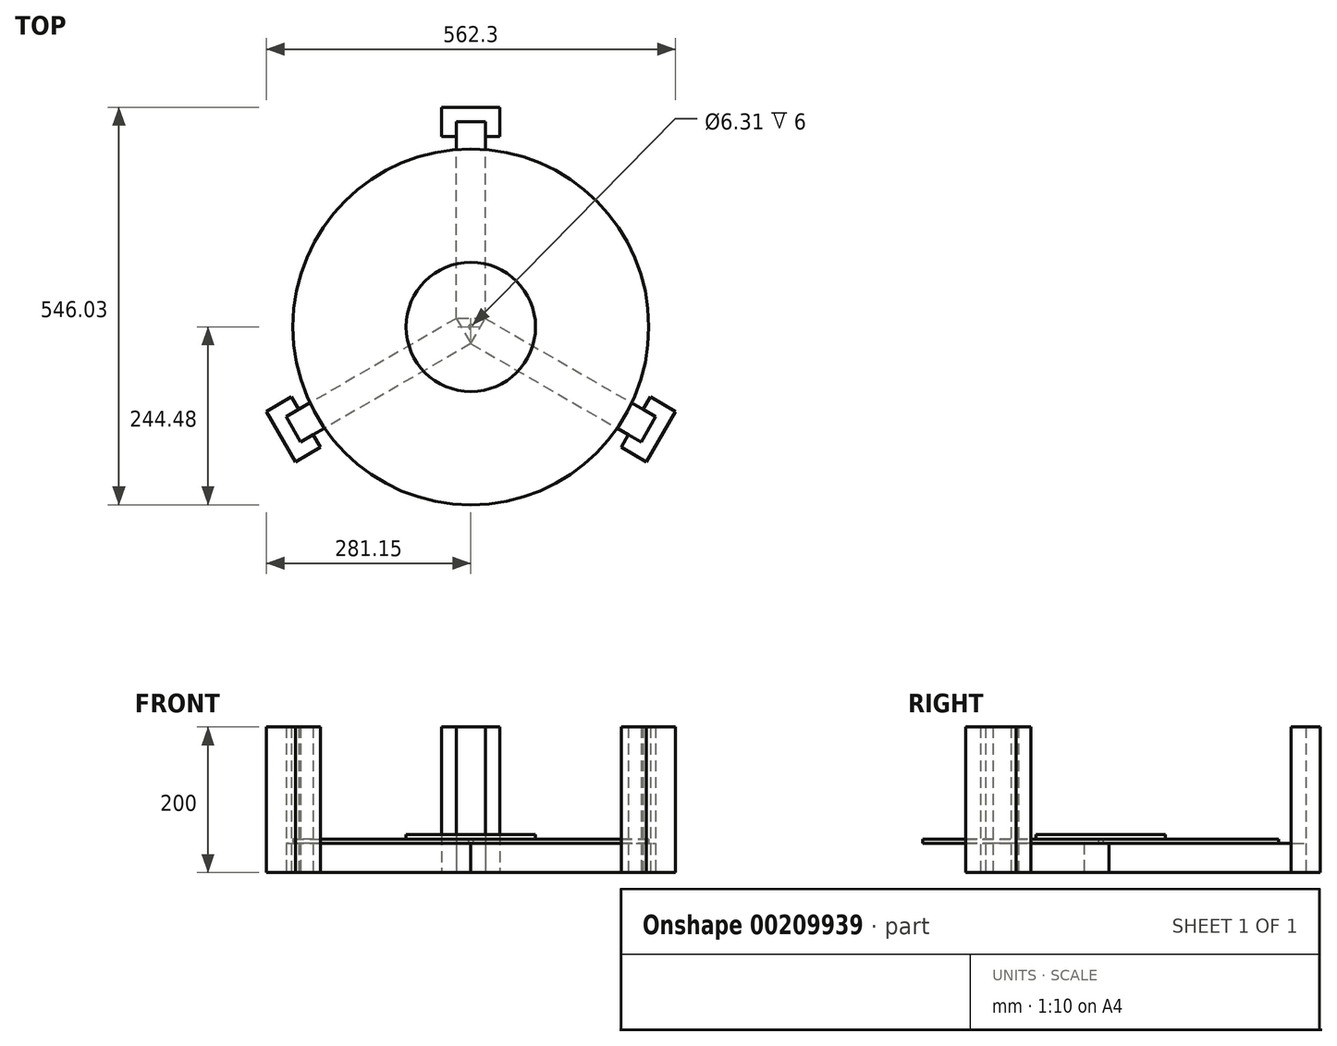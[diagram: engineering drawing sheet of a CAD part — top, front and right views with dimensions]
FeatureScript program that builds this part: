
annotation { "Feature Type Name" : "Feature", "Feature Type Description" : "" }
export const myFeature = defineFeature(function(context is Context, id is Id, definition is map)
    precondition{}
    {
        {
            var Q0;
            Q0=qCreatedBy(makeId("Top.planeOp"),FACE);
            var sketch = newSketch(context, id + "F0", { "sketchPlane" : qUnion([Q0])});
            skLineSegment(sketch, "E0.bottom", {"start": v(0, 0) * mm, "end": v(-20, 0) * mm});
            skLineSegment(sketch, "E0.top", {"start": v(0, 270) * mm, "end": v(-20, 270) * mm});
            skLineSegment(sketch, "E0.left", {"start": v(0, 0) * mm, "end": v(0, 270) * mm});
            skLineSegment(sketch, "E0.right", {"start": v(-20, 0) * mm, "end": v(-20, 270) * mm});
            skLineSegment(sketch, "E1.bottom", {"start": v(0, 0) * mm, "end": v(20, 0) * mm});
            skLineSegment(sketch, "E1.top", {"start": v(0, 270) * mm, "end": v(20, 270) * mm});
            skLineSegment(sketch, "E1.right", {"start": v(20, 0) * mm, "end": v(20, 270) * mm});
            skSolve(sketch);
        }
        {
            var Q0;
            Q0=makeQuery(id+"F0.imprint","IMPRINT",FACE,{"disambiguationData":[TD([[makeQuery(id+"F0.imprint","IMPRINT",EDGE,{"derivedFrom":sQuery(id+"F0.wireOp",EDGE,"E0.bottom")}),-1.0]])]});
            var Q1;
            Q1=makeQuery(id+"F0.imprint","IMPRINT",FACE,{"disambiguationData":[TD([[makeQuery(id+"F0.imprint","IMPRINT",EDGE,{"derivedFrom":sQuery(id+"F0.wireOp",EDGE,"E1.bottom")}),1.0]])]});
            extrude(context, id + "F1", {"entities" : qUnion([Q0, Q1]), "depth" : 40 * mm});
        }
        {
            var Q0;
            Q0=makeQuery(id+"F1.opExtrude","SWEPT_BODY",BODY,{"disambiguationData":[OSD([sQuery(id+"F0.wireOp",EDGE,"E0.bottom"),sQuery(id+"F0.wireOp",EDGE,"E0.top"),sQuery(id+"F0.wireOp",EDGE,"E0.right"),sQuery(id+"F0.wireOp",EDGE,"E1.bottom"),sQuery(id+"F0.wireOp",EDGE,"E1.top"),sQuery(id+"F0.wireOp",EDGE,"E1.right")])]});
            var Q1;
            Q1=makeQuery(id+"F1.opExtrude","CAP_EDGE",EDGE,{"disambiguationData":[OSD([sQuery(id+"F0.wireOp",EDGE,"E0.bottom"),sQuery(id+"F0.wireOp",EDGE,"E1.bottom")])],"isStart":false});
            transform(context, id + "F2", {"entities" : qUnion([Q0]), "transformType" : TransformType.TRANSLATION_DISTANCE, "transformDirection" : qUnion([Q1]), "distance" : 40 * mm, "oppositeDirection" : true, "makeCopy" : true});
        }
        {
            var Q0;
            Q0=makeQuery(id+"F2.opPattern","COPY",BODY,{"derivedFrom":makeQuery(id+"F1.opExtrude","SWEPT_BODY",BODY,{"disambiguationData":[OSD([sQuery(id+"F0.wireOp",EDGE,"E0.bottom"),sQuery(id+"F0.wireOp",EDGE,"E0.top"),sQuery(id+"F0.wireOp",EDGE,"E0.right"),sQuery(id+"F0.wireOp",EDGE,"E1.bottom"),sQuery(id+"F0.wireOp",EDGE,"E1.top"),sQuery(id+"F0.wireOp",EDGE,"E1.right")])]}),"instanceName":"1"});
            var Q1;
            Q1=makeQuery(id+"F1.opExtrude","SWEPT_EDGE",EDGE,{"disambiguationData":[OSD([sQuery(id+"F0.wireOp",EDGE,"E1.bottom"),sQuery(id+"F0.wireOp",EDGE,"E1.right")])]});
            transform(context, id + "F3", {"entities" : qUnion([Q0]), "transformType" : TransformType.ROTATION, "transformAxis" : qUnion([Q1]), "angle" : 120 * degree, "makeCopy" : false});
        }
        {
            var Q0;
            Q0=makeQuery(id+"F2.opPattern","COPY",BODY,{"derivedFrom":makeQuery(id+"F1.opExtrude","SWEPT_BODY",BODY,{"disambiguationData":[OSD([sQuery(id+"F0.wireOp",EDGE,"E0.bottom"),sQuery(id+"F0.wireOp",EDGE,"E0.top"),sQuery(id+"F0.wireOp",EDGE,"E0.right"),sQuery(id+"F0.wireOp",EDGE,"E1.bottom"),sQuery(id+"F0.wireOp",EDGE,"E1.top"),sQuery(id+"F0.wireOp",EDGE,"E1.right")])]}),"instanceName":"1"});
            var Q1;
            Q1=makeQuery(id+"F2.opPattern","COPY",EDGE,{"derivedFrom":makeQuery(id+"F1.opExtrude","CAP_EDGE",EDGE,{"disambiguationData":[OSD([sQuery(id+"F0.wireOp",EDGE,"E0.bottom"),sQuery(id+"F0.wireOp",EDGE,"E1.bottom")])],"isStart":false}),"instanceName":"1"});
            transform(context, id + "F4", {"entities" : qUnion([Q0]), "transformType" : TransformType.TRANSLATION_DISTANCE, "transformDirection" : qUnion([Q1]), "distance" : 40 * mm, "oppositeDirection" : true, "makeCopy" : true});
        }
        {
            var Q0;
            Q0=makeQuery(id+"F4.opPattern","COPY",BODY,{"derivedFrom":makeQuery(id+"F2.opPattern","COPY",BODY,{"derivedFrom":makeQuery(id+"F1.opExtrude","SWEPT_BODY",BODY,{"disambiguationData":[OSD([sQuery(id+"F0.wireOp",EDGE,"E0.bottom"),sQuery(id+"F0.wireOp",EDGE,"E0.top"),sQuery(id+"F0.wireOp",EDGE,"E0.right"),sQuery(id+"F0.wireOp",EDGE,"E1.bottom"),sQuery(id+"F0.wireOp",EDGE,"E1.top"),sQuery(id+"F0.wireOp",EDGE,"E1.right")])]}),"instanceName":"1"}),"instanceName":"1"});
            var Q1;
            Q1=makeQuery(id+"F2.opPattern","COPY",EDGE,{"derivedFrom":makeQuery(id+"F1.opExtrude","SWEPT_EDGE",EDGE,{"disambiguationData":[OSD([sQuery(id+"F0.wireOp",EDGE,"E1.bottom"),sQuery(id+"F0.wireOp",EDGE,"E1.right")])]}),"instanceName":"1"});
            transform(context, id + "F5", {"entities" : qUnion([Q0]), "transformType" : TransformType.ROTATION, "transformAxis" : qUnion([Q1]), "angle" : 120 * degree, "makeCopy" : false});
        }
        {
            var Q0;
            Q0=qCreatedBy(makeId("Top.planeOp"),FACE);
            var sketch = newSketch(context, id + "F6", { "sketchPlane" : qUnion([Q0])});
            skLineSegment(sketch, "E2", {"start": v(0, 0) * mm, "end": v(0, -34.64) * mm});
            skLineSegment(sketch, "E3", {"start": v(0, 0) * mm, "end": v(-20, 0) * mm});
            skLineSegment(sketch, "E4", {"start": v(0, 0) * mm, "end": v(20, 0) * mm});
            skLineSegment(sketch, "E5", {"start": v(-20, 0) * mm, "end": v(0, -34.64) * mm});
            skLineSegment(sketch, "E6", {"start": v(20, 0) * mm, "end": v(0, -34.64) * mm});
            skLineSegment(sketch, "E7", {"start": v(10, -17.32) * mm, "end": v(-20, 0) * mm});
            skLineSegment(sketch, "E8", {"start": v(20, 0) * mm, "end": v(-10, -17.32) * mm});
            skPoint(sketch, "E9", {"position": v(0, -11.55) * mm});
            skCircle(sketch, "E10", {"center": v(0, -11.55) * mm, "radius": 244.47 * mm});
            skCircle(sketch, "E11", {"center": v(0, -11.55) * mm, "radius": 3.15 * mm});
            skSolve(sketch);
        }
        {
            var Q0;
            Q0 = qSketchRegion(id + "F6", true);
            var Q1;
            {var subQ0=sQuery(id+"F6.wireOp",EDGE,"E6");var subQ3=sQuery(id+"F6.wireOp",EDGE,"E7");var subQ5=makeQuery(id+"F6.imprint","INTERSECT",VERTEX,{"derivedFrom":[subQ0,subQ3]});Q1=makeQuery(id+"F6.imprint","IMPRINT",FACE,{"disambiguationData":[TD([[makeQuery(id+"F6.imprint","IMPRINT",EDGE,{"disambiguationData":[TD([[subQ5,-1.0]])],"derivedFrom":subQ0}),-1.0]])]});}
            var Q2;
            {var subQ0=sQuery(id+"F6.wireOp",EDGE,"E5");var subQ3=sQuery(id+"F6.wireOp",EDGE,"E8");var subQ5=makeQuery(id+"F6.imprint","INTERSECT",VERTEX,{"derivedFrom":[subQ0,subQ3]});Q2=makeQuery(id+"F6.imprint","IMPRINT",FACE,{"disambiguationData":[TD([[makeQuery(id+"F6.imprint","IMPRINT",EDGE,{"disambiguationData":[TD([[subQ5,-1.0]])],"derivedFrom":subQ0}),1.0]])]});}
            var Q3;
            {var subQ1=sQuery(id+"F6.wireOp",EDGE,"E5");var subQ3=sQuery(id+"F6.wireOp",EDGE,"E8");var subQ4=makeQuery(id+"F6.imprint","INTERSECT",VERTEX,{"derivedFrom":[subQ1,subQ3]});Q3=makeQuery(id+"F6.imprint","IMPRINT",FACE,{"disambiguationData":[TD([[makeQuery(id+"F6.imprint","IMPRINT",EDGE,{"disambiguationData":[TD([[subQ4,1.0]])],"derivedFrom":subQ1}),1.0]])]});}
            var Q4;
            {var subQ0=sQuery(id+"F6.wireOp",EDGE,"E3");Q4=makeQuery(id+"F6.imprint","IMPRINT",FACE,{"disambiguationData":[TD([[makeQuery(id+"F6.imprint","IMPRINT",EDGE,{"derivedFrom":subQ0}),1.0]])]});}
            var Q5;
            {var subQ0=sQuery(id+"F6.wireOp",EDGE,"E4");Q5=makeQuery(id+"F6.imprint","IMPRINT",FACE,{"disambiguationData":[TD([[makeQuery(id+"F6.imprint","IMPRINT",EDGE,{"derivedFrom":subQ0}),-1.0]])]});}
            var Q6;
            {var subQ1=sQuery(id+"F6.wireOp",EDGE,"E6");var subQ3=sQuery(id+"F6.wireOp",EDGE,"E7");var subQ4=makeQuery(id+"F6.imprint","INTERSECT",VERTEX,{"derivedFrom":[subQ1,subQ3]});Q6=makeQuery(id+"F6.imprint","IMPRINT",FACE,{"disambiguationData":[TD([[makeQuery(id+"F6.imprint","IMPRINT",EDGE,{"disambiguationData":[TD([[subQ4,1.0]])],"derivedFrom":subQ1}),-1.0]])]});}
            extrude(context, id + "F7", {"entities" : qUnion([Q0, Q1, Q2, Q3, Q4, Q5, Q6]), "depth" : 3 * mm});
        }
        {
            var Q0;
            Q0=makeQuery(id+"F7.opExtrude","SWEPT_BODY",BODY,{"disambiguationData":[OSD([sQuery(id+"F6.wireOp",EDGE,"E3"),sQuery(id+"F6.wireOp",EDGE,"E4"),sQuery(id+"F6.wireOp",EDGE,"E5"),sQuery(id+"F6.wireOp",EDGE,"E6"),sQuery(id+"F6.wireOp",EDGE,"E10")])]});
            var Q1;
            Q1=makeQuery(id+"F4.opPattern","COPY",EDGE,{"derivedFrom":makeQuery(id+"F2.opPattern","COPY",EDGE,{"derivedFrom":makeQuery(id+"F1.opExtrude","SWEPT_EDGE",EDGE,{"disambiguationData":[OSD([sQuery(id+"F0.wireOp",EDGE,"E1.bottom"),sQuery(id+"F0.wireOp",EDGE,"E1.right")])]}),"instanceName":"1"}),"instanceName":"1"});
            transform(context, id + "F8", {"entities" : qUnion([Q0]), "transformType" : TransformType.TRANSLATION_DISTANCE, "transformDirection" : qUnion([Q1]), "distance" : 40 * mm, "oppositeDirection" : true, "makeCopy" : false});
        }
        {
            var Q0;
            Q0=makeQuery(id+"F1.opExtrude","CAP_FACE",FACE,{"disambiguationData":[OSD([sQuery(id+"F0.wireOp",EDGE,"E0.bottom"),sQuery(id+"F0.wireOp",EDGE,"E0.top"),sQuery(id+"F0.wireOp",EDGE,"E0.right"),sQuery(id+"F0.wireOp",EDGE,"E1.bottom"),sQuery(id+"F0.wireOp",EDGE,"E1.top"),sQuery(id+"F0.wireOp",EDGE,"E1.right")])],"isStart":true});
            var sketch = newSketch(context, id + "F9", { "sketchPlane" : qUnion([Q0])});
            skLineSegment(sketch, "E12.bottom", {"start": v(40, -290) * mm, "end": v(-40, -290) * mm});
            skLineSegment(sketch, "E12.left", {"start": v(40, -290) * mm, "end": v(40, -250) * mm});
            skLineSegment(sketch, "E12.right", {"start": v(-40, -290) * mm, "end": v(-40, -250) * mm});
            skLineSegment(sketch, "E13", {"start": v(20, -270) * mm, "end": v(-20, -270) * mm});
            skLineSegment(sketch, "E14", {"start": v(-20, -270) * mm, "end": v(-20, -250) * mm});
            skLineSegment(sketch, "E15", {"start": v(20, -250) * mm, "end": v(20, -270) * mm});
            skLineSegment(sketch, "E16", {"start": v(40, -250) * mm, "end": v(20, -250) * mm});
            skLineSegment(sketch, "E17", {"start": v(-20, -250) * mm, "end": v(-40, -250) * mm});
            skSolve(sketch);
        }
        {
            var Q0;
            Q0 = qSketchRegion(id + "F9", true);
            extrude(context, id + "F10", {"entities" : qUnion([Q0]), "oppositeDirection" : true, "depth" : 200 * mm});
        }
        {
            var Q0;
            Q0=makeQuery(id+"F7.opExtrude","CAP_FACE",FACE,{"disambiguationData":[OSD([sQuery(id+"F6.wireOp",EDGE,"E10"),sQuery(id+"F6.wireOp",EDGE,"E11")])],"isStart":false});
            var Q1;
            Q1=sQuery(id+"F6.wireOp",EDGE,"E11");
            extrude(context, id + "F11", {"entities" : qUnion([Q0]), "operationType" : NewBodyOperationType.ADD, "surfaceEntities" : qUnion([Q1]), "depth" : 3 * mm});
        }
        {
            var Q0;
            Q0=makeQuery(id+"F10.opExtrude","SWEPT_BODY",BODY,{"disambiguationData":[OSD([sQuery(id+"F9.wireOp",EDGE,"E12.bottom"),sQuery(id+"F9.wireOp",EDGE,"E12.left"),sQuery(id+"F9.wireOp",EDGE,"E12.right"),sQuery(id+"F9.wireOp",EDGE,"E13"),sQuery(id+"F9.wireOp",EDGE,"E14"),sQuery(id+"F9.wireOp",EDGE,"E15"),sQuery(id+"F9.wireOp",EDGE,"E16"),sQuery(id+"F9.wireOp",EDGE,"E17")])]});
            var Q1;
            Q1=makeQuery(id+"F11.opExtrude","CAP_EDGE",EDGE,{"disambiguationData":[OSD([sQuery(id+"F6.wireOp",EDGE,"E11")])],"isStart":false});
            circularPattern(context, id + "F12", {"entities" : qUnion([Q0]), "axis" : qUnion([Q1]), "angle" : 360 * degree, "instanceCount" : 3, "equalSpace" : true});
        }
        {
            var Q0;
            Q0=makeQuery(id+"F11.opExtrude","CAP_FACE",FACE,{"disambiguationData":[OSD([sQuery(id+"F6.wireOp",EDGE,"E10"),sQuery(id+"F6.wireOp",EDGE,"E11")])],"isStart":false});
            var sketch = newSketch(context, id + "F13", { "sketchPlane" : qUnion([Q0])});
            skCircle(sketch, "E18", {"center": v(0, -11.55) * mm, "radius": 88.9 * mm});
            skSolve(sketch);
        }
        {
            var Q0;
            Q0 = qSketchRegion(id + "F13", true);
            extrude(context, id + "F14", {"entities" : qUnion([Q0]), "operationType" : NewBodyOperationType.ADD, "depth" : 6.35 * mm});
        }
        {
            var Q0;
            Q0=makeQuery(id+"F2.opPattern","COPY",BODY,{"derivedFrom":makeQuery(id+"F1.opExtrude","SWEPT_BODY",BODY,{"disambiguationData":[OSD([sQuery(id+"F0.wireOp",EDGE,"E0.bottom"),sQuery(id+"F0.wireOp",EDGE,"E0.top"),sQuery(id+"F0.wireOp",EDGE,"E0.right"),sQuery(id+"F0.wireOp",EDGE,"E1.bottom"),sQuery(id+"F0.wireOp",EDGE,"E1.top"),sQuery(id+"F0.wireOp",EDGE,"E1.right")])]}),"instanceName":"1"});
            var Q1;
            Q1=makeQuery(id+"F4.opPattern","COPY",BODY,{"derivedFrom":makeQuery(id+"F2.opPattern","COPY",BODY,{"derivedFrom":makeQuery(id+"F1.opExtrude","SWEPT_BODY",BODY,{"disambiguationData":[OSD([sQuery(id+"F0.wireOp",EDGE,"E0.bottom"),sQuery(id+"F0.wireOp",EDGE,"E0.top"),sQuery(id+"F0.wireOp",EDGE,"E0.right"),sQuery(id+"F0.wireOp",EDGE,"E1.bottom"),sQuery(id+"F0.wireOp",EDGE,"E1.top"),sQuery(id+"F0.wireOp",EDGE,"E1.right")])]}),"instanceName":"1"}),"instanceName":"1"});
            var Q2;
            Q2=makeQuery(id+"F1.opExtrude","SWEPT_BODY",BODY,{"disambiguationData":[OSD([sQuery(id+"F0.wireOp",EDGE,"E0.bottom"),sQuery(id+"F0.wireOp",EDGE,"E0.top"),sQuery(id+"F0.wireOp",EDGE,"E0.right"),sQuery(id+"F0.wireOp",EDGE,"E1.bottom"),sQuery(id+"F0.wireOp",EDGE,"E1.top"),sQuery(id+"F0.wireOp",EDGE,"E1.right")])]});
            var Q3;
            Q3=makeQuery(id+"F12.opPattern","COPY",BODY,{"derivedFrom":makeQuery(id+"F10.opExtrude","SWEPT_BODY",BODY,{"disambiguationData":[OSD([sQuery(id+"F9.wireOp",EDGE,"E12.bottom"),sQuery(id+"F9.wireOp",EDGE,"E12.left"),sQuery(id+"F9.wireOp",EDGE,"E12.right"),sQuery(id+"F9.wireOp",EDGE,"E13"),sQuery(id+"F9.wireOp",EDGE,"E14"),sQuery(id+"F9.wireOp",EDGE,"E15"),sQuery(id+"F9.wireOp",EDGE,"E16"),sQuery(id+"F9.wireOp",EDGE,"E17")])]}),"instanceName":"2"});
            var Q4;
            Q4=makeQuery(id+"F12.opPattern","COPY",BODY,{"derivedFrom":makeQuery(id+"F10.opExtrude","SWEPT_BODY",BODY,{"disambiguationData":[OSD([sQuery(id+"F9.wireOp",EDGE,"E12.bottom"),sQuery(id+"F9.wireOp",EDGE,"E12.left"),sQuery(id+"F9.wireOp",EDGE,"E12.right"),sQuery(id+"F9.wireOp",EDGE,"E13"),sQuery(id+"F9.wireOp",EDGE,"E14"),sQuery(id+"F9.wireOp",EDGE,"E15"),sQuery(id+"F9.wireOp",EDGE,"E16"),sQuery(id+"F9.wireOp",EDGE,"E17")])]}),"instanceName":"1"});
            var Q5;
            Q5=makeQuery(id+"F10.opExtrude","SWEPT_BODY",BODY,{"disambiguationData":[OSD([sQuery(id+"F9.wireOp",EDGE,"E12.bottom"),sQuery(id+"F9.wireOp",EDGE,"E12.left"),sQuery(id+"F9.wireOp",EDGE,"E12.right"),sQuery(id+"F9.wireOp",EDGE,"E13"),sQuery(id+"F9.wireOp",EDGE,"E14"),sQuery(id+"F9.wireOp",EDGE,"E15"),sQuery(id+"F9.wireOp",EDGE,"E16"),sQuery(id+"F9.wireOp",EDGE,"E17")])]});
            var Q6;
            Q6=makeQuery(id+"F7.opExtrude","SWEPT_BODY",BODY,{"disambiguationData":[OSD([sQuery(id+"F6.wireOp",EDGE,"E10"),sQuery(id+"F6.wireOp",EDGE,"E11")])]});
            transform(context, id + "F15", {"entities" : qUnion([Q0, Q1, Q2, Q3, Q4, Q5, Q6]), "transformType" : TransformType.TRANSLATION_3D, "dx" : 0 * mm, "dy" : 11.55 * mm, "dz" : 0 * mm, "makeCopy" : false});
        }
    });
